# Revit family: 1Construction_Fences-&-Traffic-Security_AutoGate_Chainlink-Pivot-Gates
name_source: partatom
category: Specialty Equipment
units: mm (PartAtom-declared; Revit-internal decimal feet)

## family parameters
Always vertical = Yes
Cut with Voids When Loaded = No
Enable Cutting in Views = Yes
Maintain Annotation Orientation = No
OmniClass Number = 23.25.40.21.21
OmniClass Title = Gates
Part Type = Normal
Room Calculation Point = No
Round Connector Dimension = Use Diameter
Shared = No
Work Plane-Based = Yes

## types (2) — shared parameters
Assembly Code = G2040100
Date Updated = -
Description = Chainlink Vertcal Pivot Gate
Installation instructions = https://www.itwredhead.com
Keynote = 323100
Manufacturer = AutoGate
Product Documentation Link = https://www.itwredhead.com
Product Page URL = https://www.autogate.com
Product data url = https://www.bimobject.com
URL = https://www.autogate.com
Version = 1
zero-valued in all types: Default Elevation

## per-type parameters (varying)
| type | Model | z_Barb Wire Visibility | z_Type Index |
| Chainlink VPG with Barb Wire | Chainlink - VPG - Barb Wire | Yes | 2 |
| Chainlink VPG Flat Top | Chainlink - VPG - Flat Top | No | 1 |

## geometry (parser evidence)
native form markers: Sweep x7
no freeform markers — native parametric forms only
